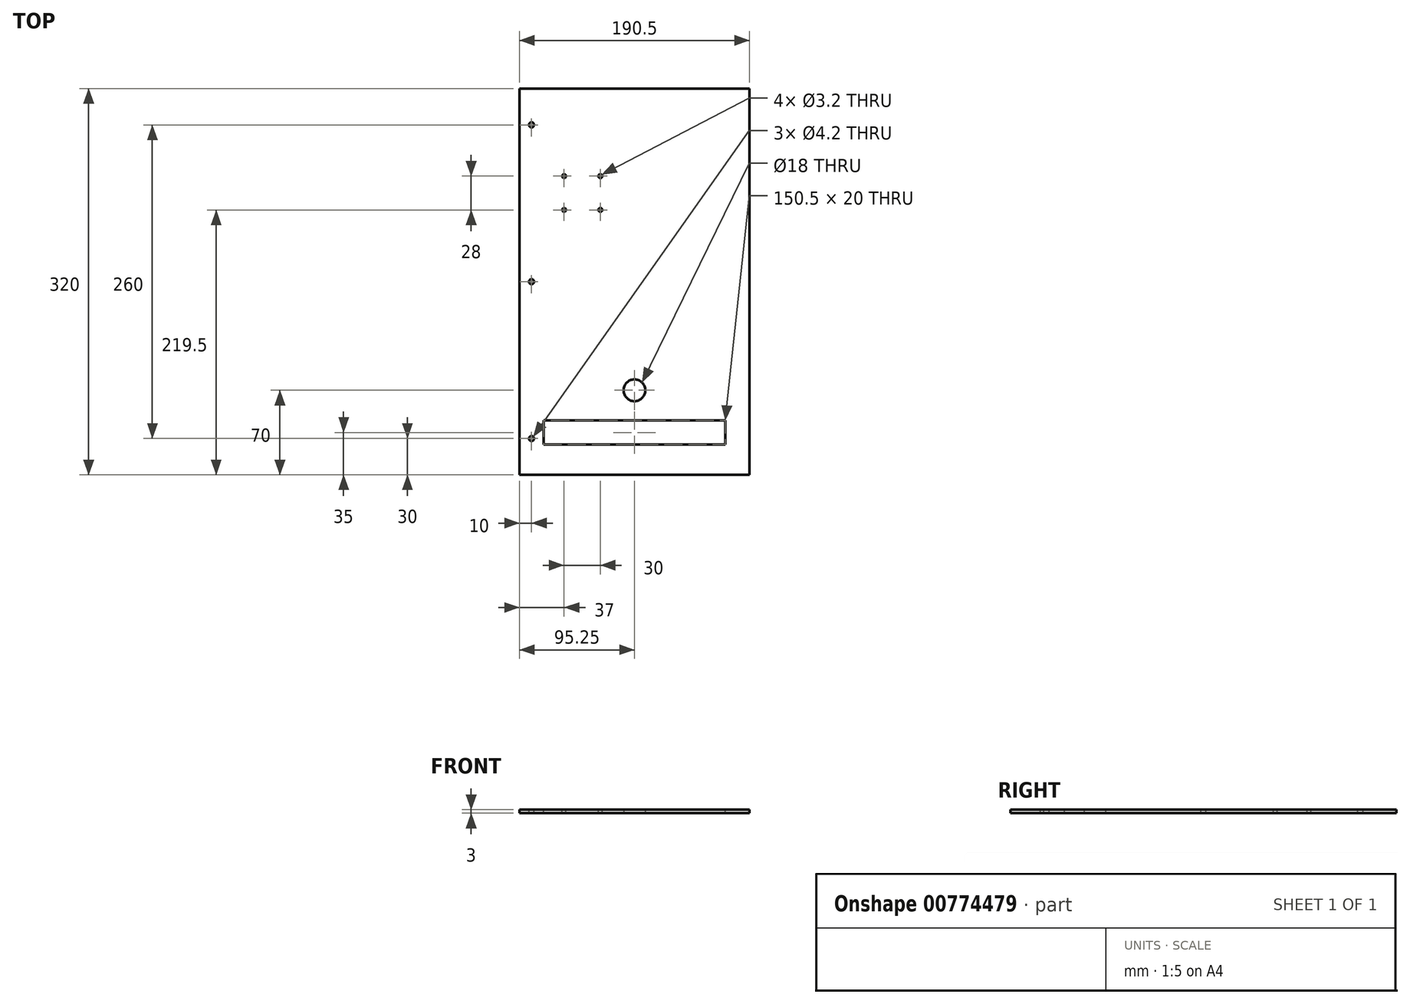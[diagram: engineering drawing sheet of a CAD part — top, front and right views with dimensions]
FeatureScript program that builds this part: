
annotation { "Feature Type Name" : "Feature", "Feature Type Description" : "" }
export const myFeature = defineFeature(function(context is Context, id is Id, definition is map)
    precondition{}
    {
        {
            assignVariable(context, id + "F0", {"name" : "Epaisseur", "anyValue" : 3});
        }
        {
            var Q0;
            Q0=qCreatedBy(makeId("Top.planeOp"),FACE);
            var sketch = newSketch(context, id + "F1", { "sketchPlane" : qUnion([Q0])});
            skLineSegment(sketch, "E0.bottom", {"start": v(-95.25, -160) * mm, "end": v(95.25, -160) * mm});
            skLineSegment(sketch, "E0.top", {"start": v(-95.25, 160) * mm, "end": v(95.25, 160) * mm});
            skLineSegment(sketch, "E0.left", {"start": v(-95.25, -160) * mm, "end": v(-95.25, 160) * mm});
            skLineSegment(sketch, "E0.right", {"start": v(95.25, -160) * mm, "end": v(95.25, 160) * mm});
            skPoint(sketch, "E0.middle", {"position": v(0, 0) * mm});
            skSolve(sketch);
        }
        {
            var Q0;
            Q0=makeQuery(id+"F1.imprint","IMPRINT",FACE,{"disambiguationData":[TD([[makeQuery(id+"F1.imprint","IMPRINT",EDGE,{"derivedFrom":sQuery(id+"F1.wireOp",EDGE,"E0.bottom")}),1.0]])]});
            extrude(context, id + "F2", {"entities" : qUnion([Q0]), "depth" : (getVariable(context, 'Epaisseur')) * mm, "offsetDistance" : 25 * mm});
        }
        {
            var Q0;
            Q0=makeQuery(id+"F2.opExtrude","CAP_FACE",FACE,{"disambiguationData":[OSD([sQuery(id+"F1.wireOp",EDGE,"E0.bottom"),sQuery(id+"F1.wireOp",EDGE,"E0.top"),sQuery(id+"F1.wireOp",EDGE,"E0.left"),sQuery(id+"F1.wireOp",EDGE,"E0.right")])],"isStart":false});
            var sketch = newSketch(context, id + "F3", { "sketchPlane" : qUnion([Q0])});
            skLineSegment(sketch, "E1", {"start": v(-85.25, 160) * mm, "end": v(-85.25, -160) * mm, "construction": true});
            skPoint(sketch, "E2", {"position": v(-85.25, 130) * mm});
            skPoint(sketch, "E3", {"position": v(-85.25, 0) * mm});
            skPoint(sketch, "E4", {"position": v(-85.25, -130) * mm});
            skSolve(sketch);
        }
        {
            var Q0;
            Q0=sQuery(id+"F3.wireOp",VERTEX,"E2");
            var Q1;
            Q1=sQuery(id+"F3.wireOp",VERTEX,"E3");
            var Q2;
            Q2=sQuery(id+"F3.wireOp",VERTEX,"E4");
            var Q3;
            Q3=makeQuery(id+"F2.opExtrude","SWEPT_BODY",BODY,{"disambiguationData":[OSD([sQuery(id+"F1.wireOp",EDGE,"E0.bottom"),sQuery(id+"F1.wireOp",EDGE,"E0.top"),sQuery(id+"F1.wireOp",EDGE,"E0.left"),sQuery(id+"F1.wireOp",EDGE,"E0.right")])]});
            hole(context, id + "F4", {"style" : HoleStyle.SIMPLE, "endStyle" : HoleEndStyle.BLIND, "holeDiameter" : 4.2 * mm, "majorDiameter" : 5 * mm, "holeDepth" : 4 * mm, "isTappedThrough" : true, "tappedDepth" : 2.3 * mm, "tapClearance" : 3, "startFromSketch" : true, "locations" : qUnion([Q0, Q1, Q2]), "scope" : qUnion([Q3])});
        }
        {
            var Q0;
            Q0=makeQuery(id+"F2.opExtrude","CAP_FACE",FACE,{"disambiguationData":[OSD([sQuery(id+"F1.wireOp",EDGE,"E0.bottom"),sQuery(id+"F1.wireOp",EDGE,"E0.top"),sQuery(id+"F1.wireOp",EDGE,"E0.left"),sQuery(id+"F1.wireOp",EDGE,"E0.right")])],"isStart":false});
            var sketch = newSketch(context, id + "F5", { "sketchPlane" : qUnion([Q0])});
            skLineSegment(sketch, "E5.bottom", {"start": v(-58.25, 87.5) * mm, "end": v(-28.25, 87.5) * mm, "construction": true});
            skLineSegment(sketch, "E5.top", {"start": v(-58.25, 59.5) * mm, "end": v(-28.25, 59.5) * mm, "construction": true});
            skLineSegment(sketch, "E5.left", {"start": v(-58.25, 87.5) * mm, "end": v(-58.25, 59.5) * mm, "construction": true});
            skLineSegment(sketch, "E5.right", {"start": v(-28.25, 87.5) * mm, "end": v(-28.25, 59.5) * mm, "construction": true});
            skSolve(sketch);
        }
        {
            var Q0;
            Q0=sQuery(id+"F5.wireOp",VERTEX,"E5.bottom.start");
            var Q1;
            Q1=sQuery(id+"F5.wireOp",VERTEX,"E5.top.start");
            var Q2;
            Q2=sQuery(id+"F5.wireOp",VERTEX,"E5.top.end");
            var Q3;
            Q3=sQuery(id+"F5.wireOp",VERTEX,"E5.bottom.end");
            var Q4;
            Q4=makeQuery(id+"F2.opExtrude","SWEPT_BODY",BODY,{"disambiguationData":[OSD([sQuery(id+"F1.wireOp",EDGE,"E0.bottom"),sQuery(id+"F1.wireOp",EDGE,"E0.top"),sQuery(id+"F1.wireOp",EDGE,"E0.left"),sQuery(id+"F1.wireOp",EDGE,"E0.right")])]});
            hole(context, id + "F6", {"style" : HoleStyle.SIMPLE, "endStyle" : HoleEndStyle.BLIND, "holeDiameter" : 3.2 * mm, "majorDiameter" : 5 * mm, "holeDepth" : 4 * mm, "isTappedThrough" : true, "tappedDepth" : 2.3 * mm, "tapClearance" : 3, "startFromSketch" : true, "locations" : qUnion([Q0, Q1, Q2, Q3]), "scope" : qUnion([Q4])});
        }
        {
            var Q0;
            Q0=makeQuery(id+"F2.opExtrude","CAP_FACE",FACE,{"disambiguationData":[OSD([sQuery(id+"F1.wireOp",EDGE,"E0.bottom"),sQuery(id+"F1.wireOp",EDGE,"E0.top"),sQuery(id+"F1.wireOp",EDGE,"E0.left"),sQuery(id+"F1.wireOp",EDGE,"E0.right")])],"isStart":false});
            var sketch = newSketch(context, id + "F7", { "sketchPlane" : qUnion([Q0])});
            skLineSegment(sketch, "E6.bottom", {"start": v(-75.25, -135) * mm, "end": v(75.25, -135) * mm});
            skLineSegment(sketch, "E6.top", {"start": v(-75.25, -115) * mm, "end": v(75.25, -115) * mm});
            skLineSegment(sketch, "E6.left", {"start": v(-75.25, -135) * mm, "end": v(-75.25, -115) * mm});
            skLineSegment(sketch, "E6.right", {"start": v(75.25, -135) * mm, "end": v(75.25, -115) * mm});
            skPoint(sketch, "E6.middle", {"position": v(0, -125) * mm});
            skSolve(sketch);
        }
        {
            var Q0;
            Q0=makeQuery(id+"F7.imprint","IMPRINT",FACE,{"disambiguationData":[TD([[makeQuery(id+"F7.imprint","IMPRINT",EDGE,{"derivedFrom":sQuery(id+"F7.wireOp",EDGE,"E6.bottom")}),1.0]])]});
            extrude(context, id + "F8", {"entities" : qUnion([Q0]), "operationType" : NewBodyOperationType.REMOVE, "oppositeDirection" : true, "depth" : 25 * mm, "offsetDistance" : 25 * mm});
        }
        {
            var Q0;
            Q0=makeQuery(id+"F2.opExtrude","CAP_FACE",FACE,{"disambiguationData":[OSD([sQuery(id+"F1.wireOp",EDGE,"E0.bottom"),sQuery(id+"F1.wireOp",EDGE,"E0.top"),sQuery(id+"F1.wireOp",EDGE,"E0.left"),sQuery(id+"F1.wireOp",EDGE,"E0.right")])],"isStart":true});
            var sketch = newSketch(context, id + "F9", { "sketchPlane" : qUnion([Q0])});
            skCircle(sketch, "E7", {"center": v(0, 90) * mm, "radius": 9 * mm});
            skSolve(sketch);
        }
        {
            var Q0;
            Q0 = qSketchRegion(id + "F9", true);
            extrude(context, id + "F10", {"entities" : qUnion([Q0]), "operationType" : NewBodyOperationType.REMOVE, "endBound" : BoundingType.UP_TO_NEXT, "oppositeDirection" : true, "depth" : 25 * mm, "offsetDistance" : 25 * mm});
        }
    });
